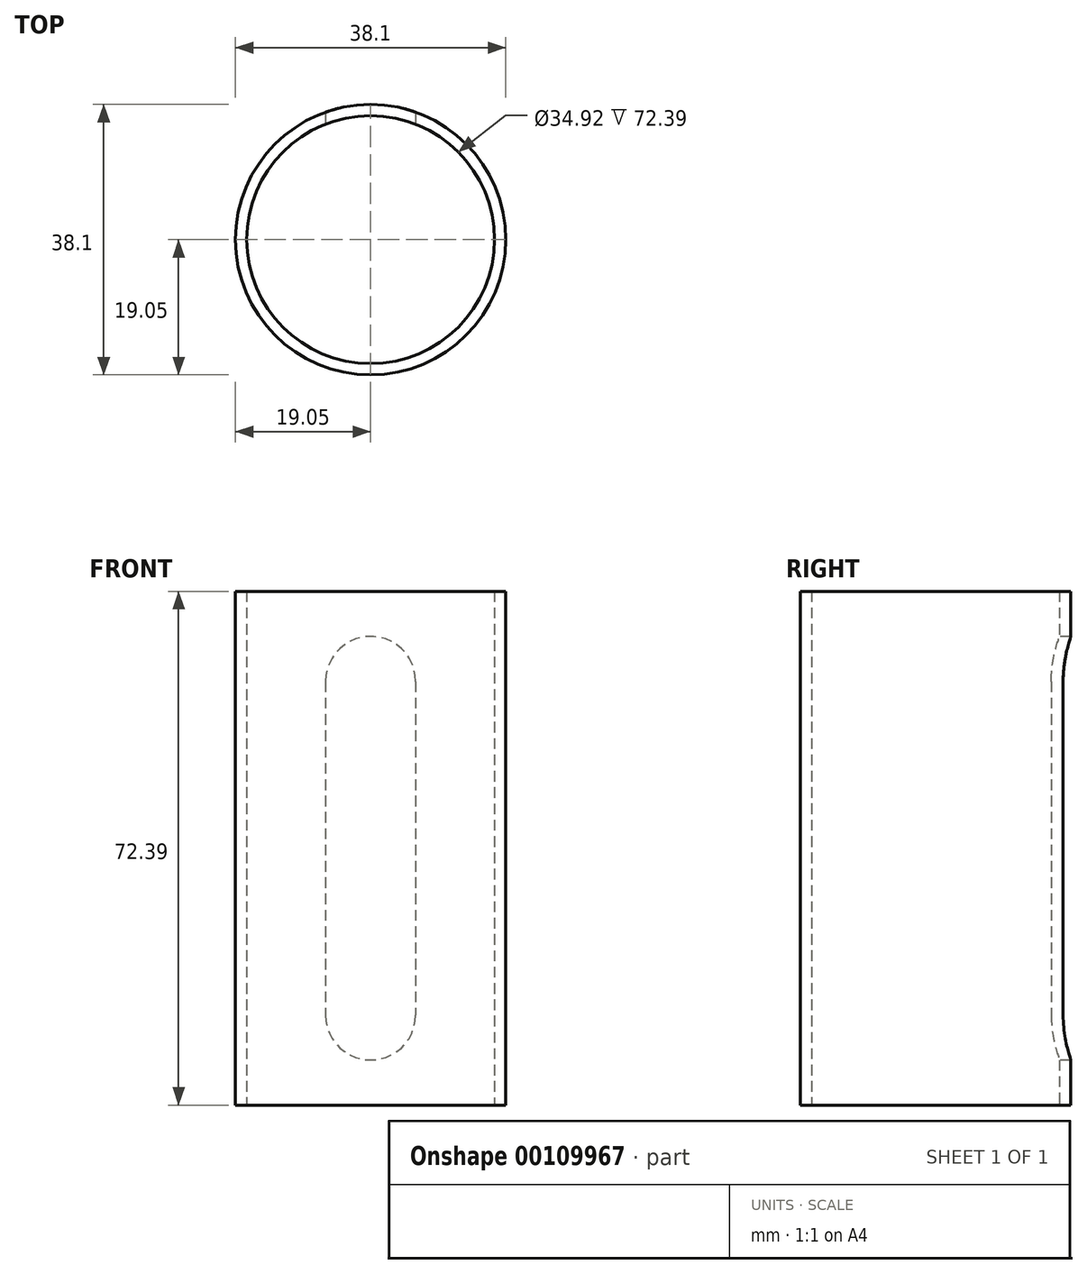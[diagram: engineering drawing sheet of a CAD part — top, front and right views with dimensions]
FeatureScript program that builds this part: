
annotation { "Feature Type Name" : "Feature", "Feature Type Description" : "" }
export const myFeature = defineFeature(function(context is Context, id is Id, definition is map)
    precondition{}
    {
        {
            var Q0;
            Q0=qCreatedBy(makeId("Top.planeOp"),FACE);
            var sketch = newSketch(context, id + "F0", { "sketchPlane" : qUnion([Q0])});
            skCircle(sketch, "E0", {"center": v(0, 0) * mm, "radius": 19.05 * mm});
            skCircle(sketch, "E1", {"center": v(0, 0) * mm, "radius": 17.46 * mm});
            skSolve(sketch);
        }
        {
            var Q0;
            Q0 = qSketchRegion(id + "F0", true);
            extrude(context, id + "F1", {"entities" : qUnion([Q0]), "depth" : 72.39 * mm});
        }
        {
            var Q0;
            Q0=qCreatedBy(makeId("Front.planeOp"),FACE);
            var sketch = newSketch(context, id + "F2", { "sketchPlane" : qUnion([Q0])});
            skLineSegment(sketch, "E2", {"start": v(0, 59.7) * mm, "end": v(0, 12.7) * mm, "construction": true});
            skArc(sketch, "E3", {"start": v(-6.35, 12.7) * mm, "mid": v(0, 6.35) * mm, "end": v(6.35, 12.7) * mm});
            skLineSegment(sketch, "E4", {"start": v(6.35, 59.7) * mm, "end": v(6.35, 12.7) * mm});
            skLineSegment(sketch, "E5", {"start": v(-6.35, 59.7) * mm, "end": v(-6.35, 12.7) * mm});
            skArc(sketch, "E6", {"start": v(-6.35, 59.7) * mm, "mid": v(0, 66.04) * mm, "end": v(6.35, 59.7) * mm});
            skSolve(sketch);
        }
        {
            var Q0;
            Q0 = qSketchRegion(id + "F2", true);
            extrude(context, id + "F3", {"entities" : qUnion([Q0]), "operationType" : NewBodyOperationType.REMOVE, "oppositeDirection" : true, "depth" : 25.4 * mm});
        }
    });
